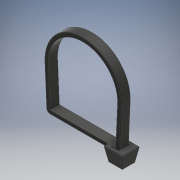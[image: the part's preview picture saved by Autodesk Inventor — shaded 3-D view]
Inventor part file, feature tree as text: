
AUTODESK INVENTOR PART (.ipt)
format: ipt  version: 2018 (Build 220112000, 112)  size: 280,064 bytes
history: native  units: mm
features: extrude x4, sketch x4, projected_geometry x3, chamfer x1, fillet x1
ambient origin geometry x8: Origin, YZ Plane, XZ Plane, XY Plane, X Axis, Y Axis, Z Axis, Center Point
bodies: Solid1 (feature_tree)
feature tree (13):
  extrude  "Extrusion1"  Depth=1.6mm
  extrude  "Extrusion2"  Depth=1.016mm
  chamfer  "Chamfer1"  Distance=2.5mm
  extrude  "Extrusion3"  Depth=1.8mm
  fillet  "Fillet1"  Radius=4.9mm
  extrude  "Extrusion4"  Depth=0.2mm
  sketch  "Sketch1"  dims[d0=18.3mm d2=1.6mm]
  sketch  "Sketch2"  dims[d3=19.0mm d4=1.016mm d5=2.5mm d6=0.0mm]
  projected_geometry  "Projected Loop1"
  sketch  "Sketch3"  dims[d10=4.6mm d11=0.0mm d12=1.8mm d13=4.9mm]
  projected_geometry  "Projected Loop2"
  sketch  "Sketch4"  dims[d14=3.7mm d15=13.962634mm d16=0.6mm d17=2.0mm d18=13.962634mm d19=0.6mm d20=1.0mm d21=0.2mm d22=0.2mm d23=2.0mm d24=0.0mm d25=0.2mm d26=2.0mm d27=0.0mm d28=2.5mm d29=3.0mm]
  projected_geometry  "Projected Loop3"
